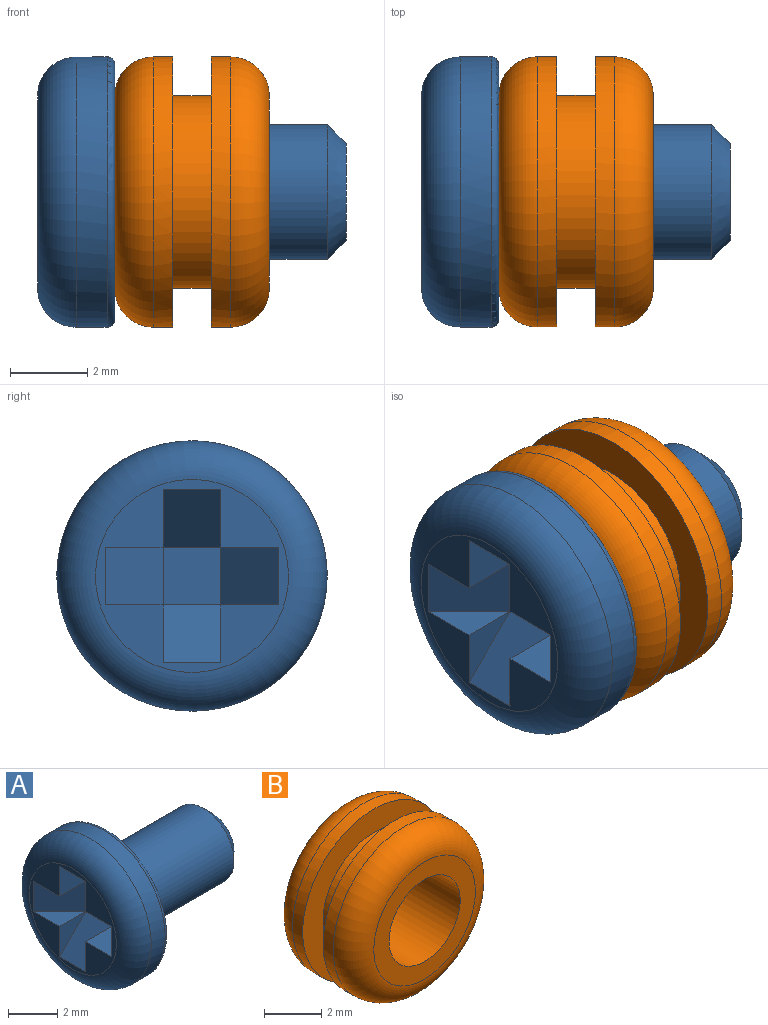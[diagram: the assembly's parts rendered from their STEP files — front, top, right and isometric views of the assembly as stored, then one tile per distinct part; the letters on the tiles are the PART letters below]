
ASSEMBLY  parts=2 mates=1
PART A: 22 faces, bbox 8x7.6x7.6 mm
  f0: plane 5x5mm, normal (-1,0,0), area 8.4mm2, adj f8,f9,f10,f11,f12,f13,f14,f15
  f1: plane 2.5x2.5mm, normal (1,0,0), area 4.9mm2, adj f5
  f2: cylinder r=1.75mm len=5.3mm, axis (1,0,0), area 58.3mm2, adj f5,f6
  f3: plane 6.6x6.6mm, normal (1,0,0), area 22.3mm2, adj f6,f7
  f4: cylinder r=3.5mm len=7mm, axis (1,0,0), area 17.6mm2, adj f7,f8
  f5: cone r=1.25mm half-angle=45deg, axis (-1,0,0), area 6.7mm2, adj f1,f2
  f6: torus R=1.95mm, axis (-1,0,0), area 3.6mm2, adj f2,f3
  f7: torus R=3.3mm, axis (-1,0,0), area 6.8mm2, adj f3,f4
  f8: torus R=2.5mm, axis (1,0,0), area 31mm2, adj f0,f4
  f9: plane 1.5x1.5mm, normal (0,0,-1), area 1.1mm2, adj f0,f16,f21
  f10: plane 1.5x1.5mm, normal (0,0,1), area 1.1mm2, adj f0,f11,f21
  f11: plane 1.5x1.5mm, normal (0,-1,0), area 1.1mm2, adj f0,f10,f19
  f12: plane 1.5x1.5mm, normal (0,1,0), area 1.1mm2, adj f0,f13,f19
  f13: plane 1.5x1.5mm, normal (0,0,1), area 1.1mm2, adj f0,f12,f18
  f14: plane 1.5x1.5mm, normal (0,0,-1), area 1.1mm2, adj f0,f15,f18
  f15: plane 1.5x1.5mm, normal (0,1,0), area 1.1mm2, adj f0,f14,f20
  f16: plane 1.5x1.5mm, normal (0,-1,0), area 1.1mm2, adj f0,f9,f20
  f17: plane 1.5x1.5mm, normal (-1,0,0), area 2.3mm2, adj f18,f19,f20,f21
  f18: plane 1.5x1.5mm, normal (-0.71,0.71,0), area 3.2mm2, adj f0,f13,f14,f17
  f19: plane 1.5x1.5mm, normal (-0.71,0,0.71), area 3.2mm2, adj f0,f11,f12,f17
  f20: plane 1.5x1.5mm, normal (-0.71,0,-0.71), area 3.2mm2, adj f0,f15,f16,f17
  f21: plane 1.5x1.5mm, normal (-0.71,-0.71,0), area 3.2mm2, adj f0,f9,f10,f17
PART B: 10 faces, bbox 7.6x4x7.6 mm
  f0: cylinder r=3.5mm len=7mm, axis (0,1,0), area 11mm2, adj f1,f4
  f1: plane 7x7mm, normal (0,-1,0), area 18.8mm2, adj f0,f3
  f2: plane 5x5mm, normal (0,1,0), area 10mm2, adj f4,f9
  f3: cylinder r=2.5mm len=5mm, axis (0,1,0), area 15.7mm2, adj f1,f7
  f4: torus R=2.5mm, axis (0,-1,0), area 31mm2, adj f0,f2
  f5: cylinder r=3.5mm len=7mm, axis (0,1,0), area 11mm2, adj f7,f8
  f6: plane 5x5mm, normal (0,-1,0), area 10mm2, adj f8,f9
  f7: plane 7x7mm, normal (0,1,0), area 18.8mm2, adj f3,f5
  f8: torus R=2.5mm, axis (0,-1,0), area 31mm2, adj f5,f6
  f9: cylinder r=1.75mm len=4mm, axis (0,-1,0), area 44mm2, adj f2,f6
PLACE A t=(-0.1,-0.62,0.9)mm
PLACE B rot(axis=(0,0,1),90deg) t=(1.9,-0.62,0.9)mm
MATE fastened B.f0 <-> A.f2  axis (-1,0,0) through (3.9,-0.62,0.9)mm
